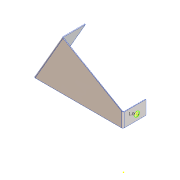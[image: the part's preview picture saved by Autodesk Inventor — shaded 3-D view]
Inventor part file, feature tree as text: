
AUTODESK INVENTOR PART (.ipt)
format: ipt  version: 2016 (Build 200138000, 138)  size: 203,264 bytes
history: native  units: in
note: dims shown in document units (in); Inventor stores cm internally (conversion verified against a paired STEP export)
features: reference x11, sheet_metal_op x7, sketch x6, other x6, fillet x1
ambient origin geometry x8: Origin, YZ Plane, XZ Plane, XY Plane, X Axis, Y Axis, Z Axis, Center Point
bodies: Solid1 (feature_tree)
feature tree (31):
  sheet_metal_op  "Face1"
  sheet_metal_op  "Flange1"
  sketch  "Sketch5"  dims[d8=3.0in]
  sheet_metal_op  "Flange2"
  fillet  "Fillet1"  Radius=30.0in
  sketch  "Sketch7"  dims[d10=90.0deg d11=13.0167in d12=0.125in d13=0.0in d14=0.125in d15=0.0625in d16=0.25in d17=0.125in d18=5.0in d19=90.0deg d20=0.125in d21=0.5in d22=0.125in d23=0.125in d24=0.125in d25=0.0625in d26=0.25in d27=0.125in d28=5.0in d29=90.0deg d30=0.125in d31=0.5in d32=0.125in d33=0.125in d36=1.063in d37=0.125in d38=0.0in d39=0.125in]
  sketch  "Sketch1"  dims[d1=30.0in]
  other  "Plate1"
  sketch  "Sketch3"  dims[d2=0.125in]
  reference  "Reference12"
  reference  "Reference13"
  reference  "Reference14"
  sketch  "Sketch4"  dims[d7=60.0deg]
  other  "Plate2"
  sheet_metal_op  "Bend1"
  sheet_metal_op  "Corner1"
  reference  "Reference15"
  reference  "Reference16"
  reference  "Reference17"
  sketch  "Sketch6"  dims[d9=180.0deg]
  other  "Plate3"
  sheet_metal_op  "Bend2"
  sheet_metal_op  "Corner2"
  reference  "Reference18"
  reference  "Reference19"
  reference  "Reference20"
  reference  "Reference21"
  reference  "Reference22"
  other  "Cut1"
  other  "Cut2"
  other  "Definition1"
